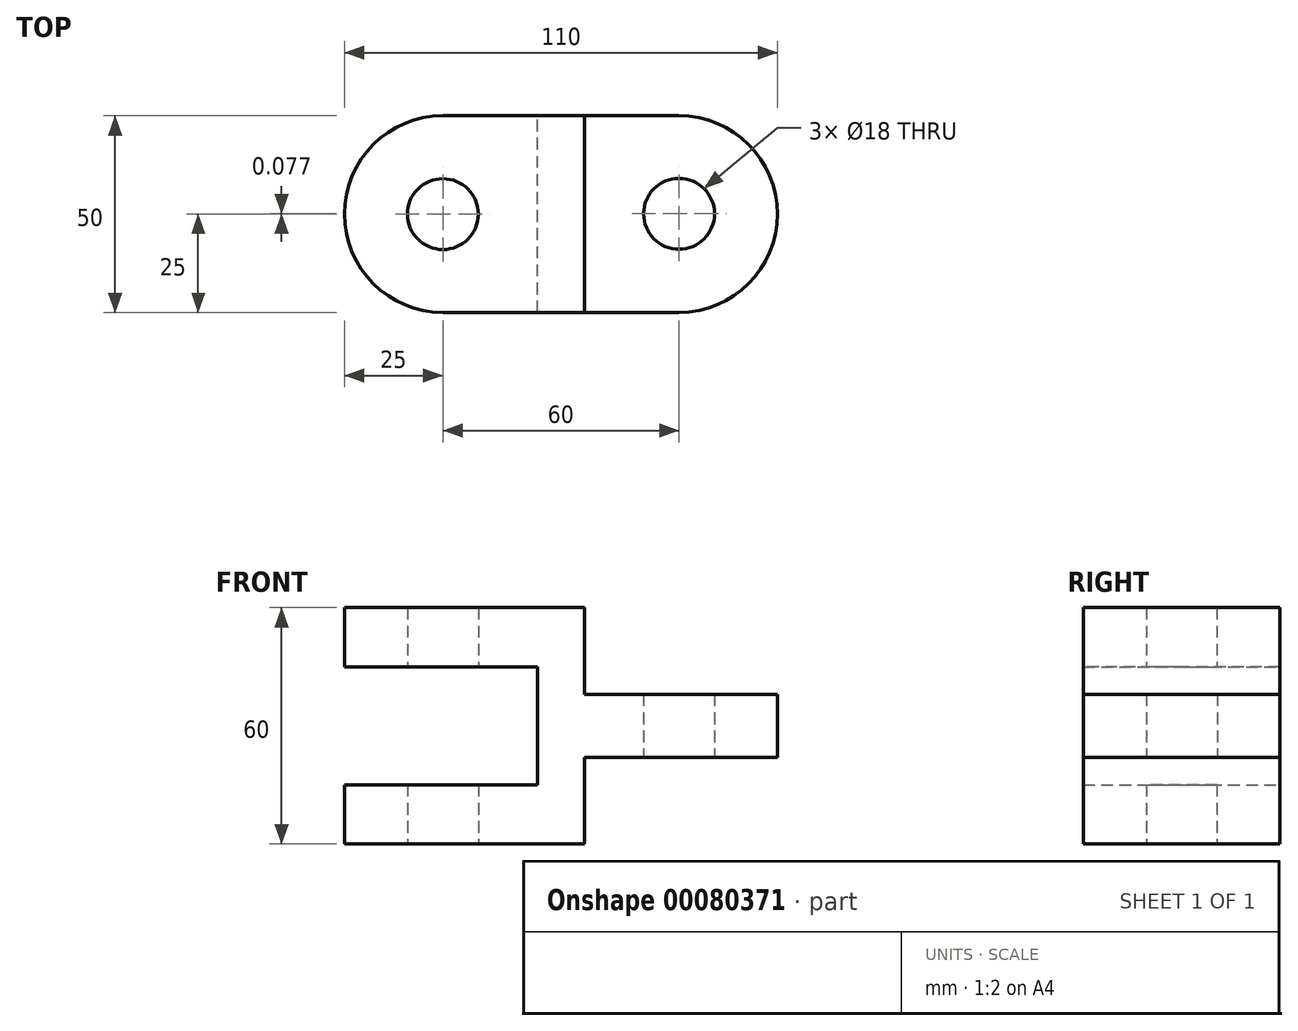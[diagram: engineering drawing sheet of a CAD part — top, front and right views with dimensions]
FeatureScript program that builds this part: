
annotation { "Feature Type Name" : "Feature", "Feature Type Description" : "" }
export const myFeature = defineFeature(function(context is Context, id is Id, definition is map)
    precondition{}
    {
        {
            var Q0;
            Q0=qCreatedBy(makeId("Front.planeOp"),FACE);
            var sketch = newSketch(context, id + "F0", { "sketchPlane" : qUnion([Q0])});
            skLineSegment(sketch, "E0.bottom", {"start": v(0, 0) * mm, "end": v(-110, 0) * mm});
            skLineSegment(sketch, "E0.top", {"start": v(0, 60) * mm, "end": v(-110, 60) * mm});
            skLineSegment(sketch, "E0.left", {"start": v(0, 0) * mm, "end": v(0, 60) * mm});
            skLineSegment(sketch, "E0.right", {"start": v(-110, 0) * mm, "end": v(-110, 60) * mm});
            skLineSegment(sketch, "E1", {"start": v(-49, 0) * mm, "end": v(-49, 22) * mm});
            skLineSegment(sketch, "E2", {"start": v(-49, 22) * mm, "end": v(0, 22) * mm});
            skLineSegment(sketch, "E3", {"start": v(-49, 60) * mm, "end": v(-49, 38) * mm});
            skLineSegment(sketch, "E4", {"start": v(-49, 38) * mm, "end": v(0, 38) * mm});
            skLineSegment(sketch, "E5", {"start": v(-110, 45) * mm, "end": v(-61, 45) * mm});
            skLineSegment(sketch, "E6", {"start": v(-61, 45) * mm, "end": v(-61, 15) * mm});
            skLineSegment(sketch, "E7", {"start": v(-61, 15) * mm, "end": v(-110, 15) * mm});
            skSolve(sketch);
        }
        {
            var Q0;
            {var subQ9=sQuery(id+"F0.wireOp",EDGE,"E1");Q0=makeQuery(id+"F0.imprint","IMPRINT",FACE,{"disambiguationData":[TD([[makeQuery(id+"F0.imprint","IMPRINT",EDGE,{"derivedFrom":subQ9}),1.0]])]});}
            extrude(context, id + "F1", {"entities" : qUnion([Q0]), "depth" : 50 * mm});
        }
        {
            var Q0;
            {var subQ0=sQuery(id+"F0.wireOp",EDGE,"E0.right");Q0=makeQuery(id+"F1.opExtrude","CAP_EDGE",EDGE,{"disambiguationData":[OSD([subQ0]),TDD([makeQuery(id+"F0.imprint","IMPRINT",EDGE,{"disambiguationData":[TD([[makeQuery(id+"F0.imprint","INTERSECT",VERTEX,{"derivedFrom":[sQuery(id+"F0.wireOp",EDGE,"E0.top"),subQ0]}),1.0]])],"derivedFrom":subQ0})])],"isStart":false});}
            var Q1;
            {var subQ0=sQuery(id+"F0.wireOp",EDGE,"E0.right");Q1=makeQuery(id+"F1.opExtrude","CAP_EDGE",EDGE,{"disambiguationData":[OSD([subQ0]),TDD([makeQuery(id+"F0.imprint","IMPRINT",EDGE,{"disambiguationData":[TD([[makeQuery(id+"F0.imprint","INTERSECT",VERTEX,{"derivedFrom":[sQuery(id+"F0.wireOp",EDGE,"E0.bottom"),subQ0]}),-1.0]])],"derivedFrom":subQ0})])],"isStart":false});}
            var Q2;
            {var subQ0=sQuery(id+"F0.wireOp",EDGE,"E0.right");Q2=makeQuery(id+"F1.opExtrude","CAP_EDGE",EDGE,{"disambiguationData":[OSD([subQ0]),TDD([makeQuery(id+"F0.imprint","IMPRINT",EDGE,{"disambiguationData":[TD([[makeQuery(id+"F0.imprint","INTERSECT",VERTEX,{"derivedFrom":[sQuery(id+"F0.wireOp",EDGE,"E0.top"),subQ0]}),1.0]])],"derivedFrom":subQ0})])],"isStart":true});}
            var Q3;
            {var subQ0=sQuery(id+"F0.wireOp",EDGE,"E0.right");Q3=makeQuery(id+"F1.opExtrude","CAP_EDGE",EDGE,{"disambiguationData":[OSD([subQ0]),TDD([makeQuery(id+"F0.imprint","IMPRINT",EDGE,{"disambiguationData":[TD([[makeQuery(id+"F0.imprint","INTERSECT",VERTEX,{"derivedFrom":[sQuery(id+"F0.wireOp",EDGE,"E0.bottom"),subQ0]}),-1.0]])],"derivedFrom":subQ0})])],"isStart":true});}
            var Q4;
            Q4=makeQuery(id+"F1.opExtrude","CAP_EDGE",EDGE,{"disambiguationData":[OSD([sQuery(id+"F0.wireOp",EDGE,"E0.left")])],"isStart":false});
            var Q5;
            Q5=makeQuery(id+"F1.opExtrude","CAP_EDGE",EDGE,{"disambiguationData":[OSD([sQuery(id+"F0.wireOp",EDGE,"E0.left")])],"isStart":true});
            fillet(context, id + "F2", {"entities" : qUnion([Q0, Q1, Q2, Q3, Q4, Q5]), "radius" : 25 * mm, "tangentPropagation" : true, "allowEdgeOverflow" : false});
        }
        {
            var Q0;
            Q0=makeQuery(id+"F1.opExtrude","SWEPT_FACE",FACE,{"disambiguationData":[OSD([sQuery(id+"F0.wireOp",EDGE,"E0.bottom")])]});
            var sketch = newSketch(context, id + "F3", { "sketchPlane" : qUnion([Q0])});
            skCircle(sketch, "E8", {"center": v(-85, 25) * mm, "radius": 9 * mm});
            skSolve(sketch);
        }
        {
            var Q0;
            Q0=makeQuery(id+"F1.opExtrude","SWEPT_FACE",FACE,{"disambiguationData":[OSD([sQuery(id+"F0.wireOp",EDGE,"E2")])]});
            var sketch = newSketch(context, id + "F4", { "sketchPlane" : qUnion([Q0])});
            skSolve(sketch);
        }
        {
            var Q0;
            Q0=makeQuery(id+"F3.imprint","IMPRINT",FACE,{"disambiguationData":[TD([[makeQuery(id+"F3.imprint","IMPRINT",EDGE,{"derivedFrom":sQuery(id+"F3.wireOp",EDGE,"E8")}),1.0]])]});
            extrude(context, id + "F5", {"entities" : qUnion([Q0]), "operationType" : NewBodyOperationType.REMOVE, "endBound" : BoundingType.THROUGH_ALL, "oppositeDirection" : true, "depth" : 25.4 * mm});
        }
        {
            var Q0;
            {var subQ0=sQuery(id+"F0.wireOp",EDGE,"E2");Q0=makeQuery(id+"F4.imprint","IMPRINT",FACE,{"disambiguationData":[TD([[makeQuery(id+"F4.imprint","IMPRINT",EDGE,{"derivedFrom":makeQuery(id+"F1.opExtrude","CAP_EDGE",EDGE,{"disambiguationData":[OSD([subQ0])],"isStart":true})}),1.0]])]});}
            var sketch = newSketch(context, id + "F6", { "sketchPlane" : qUnion([Q0])});
            skCircle(sketch, "E9", {"center": v(-25, 24.92) * mm, "radius": 9 * mm});
            skLineSegment(sketch, "E10", {"start": v(-25, 24.92) * mm, "end": v(0, 24.92) * mm, "construction": true});
            skLineSegment(sketch, "E11", {"start": v(-25, 24.92) * mm, "end": v(-26.96, 0) * mm, "construction": true});
            skSolve(sketch);
        }
        {
            var Q0;
            Q0=makeQuery(id+"F6.imprint","IMPRINT",FACE,{"disambiguationData":[TD([[makeQuery(id+"F6.imprint","IMPRINT",EDGE,{"derivedFrom":sQuery(id+"F6.wireOp",EDGE,"E9")}),1.0]])]});
            extrude(context, id + "F7", {"entities" : qUnion([Q0]), "operationType" : NewBodyOperationType.REMOVE, "oppositeDirection" : true, "depth" : 25.4 * mm});
        }
    });
